# Revit family: EH&IH HOOD
name_source: partatom
category: Generic Models
revit_build: Autodesk Revit LT 2016 (Build: 20161004_0715(x64)
units: mm (PartAtom-declared; Revit-internal decimal feet)

## family parameters
Always vertical = Yes
Can host rebar = No
Cut with Voids When Loaded = No
Part Type = Normal
Room Calculation Point = No
Round Connector Dimension = Use Diameter
Shared = No
Work Plane-Based = No

## types (11) — shared parameters
AMPs = 0
MOTOR = 0
Manufacturer = REVERSOMATIC MFC
RPM = 0
URL = http://www.reversomatic.com
WATS = 0

## per-type parameters (varying)
| type | A | AA | B | B1 | D | DU | DUS | H | Model |
| EH & IH 12 | 18" | 18" | 8 1/2" | -8 1/2" | 37" | 3" | -8 1/4" | -7 1/2" | EH & IH 12  HOOD |
| EH & IH 16 | 22" | 22" | 8 1/2" | -8 1/2" | 41" | 3" | -8 1/4" | -7 1/2" | EH & IH 16  HOOD |
| EH & IH 18 | 24" | 24" | 8 1/2" | -8 1/2" | 43" | 3" | -8 1/4" | -7 1/2" | EH & IH 18  HOOD |
| EH & IH 20 | 26" | 26" | 8 1/2" | -8 1/2" | 45" | 3" | -8 1/4" | -7 1/2" | EH & IH 20  HOOD |
| EH & IH 24 | 30" | 30" | 8 1/2" | -8 1/2" | 49" | 3" | -8 1/4" | -7 1/2" | EH & IH 24  HOOD |
| EH & IH 30 | 36" | 36" | 10 1/2" | -10 1/2" | 59" | 3" | -10 1/4" | -9 1/2" | EH & IH 30  HOOD |
| EH & IH 36 | 42" | 42" | 12" | -12" | 68" | 3" | -11 3/4" | -11" | EH & IH 36  HOOD |
| EH & IH 42 | 49" | 49" | 14 1/2" | -14 1/2" | 80" | 3 1/2" | -14 1/4" | -13 1/2" | EH & IH 42 HOOD |
| EH & IH 48 | 55" | 55" | 16" | -16" | 89" | 3 1/2" | -15 3/4" | -15" | EH & IH 48 HOOD |
| EH & IH 54 | 60" | 60" | 17 1/2" | -17 1/2" | 97" | 3" | -17 1/4" | -16 1/2" | EH & IH 54 HOOD |
| EH & IH 60 | 68" | 68" | 20" | -20" | 110" | 4" | -19 3/4" | -19" | EH & IH 60 HOOD |

## geometry (parser evidence)
native form markers: Sweep x2
no freeform markers — native parametric forms only
